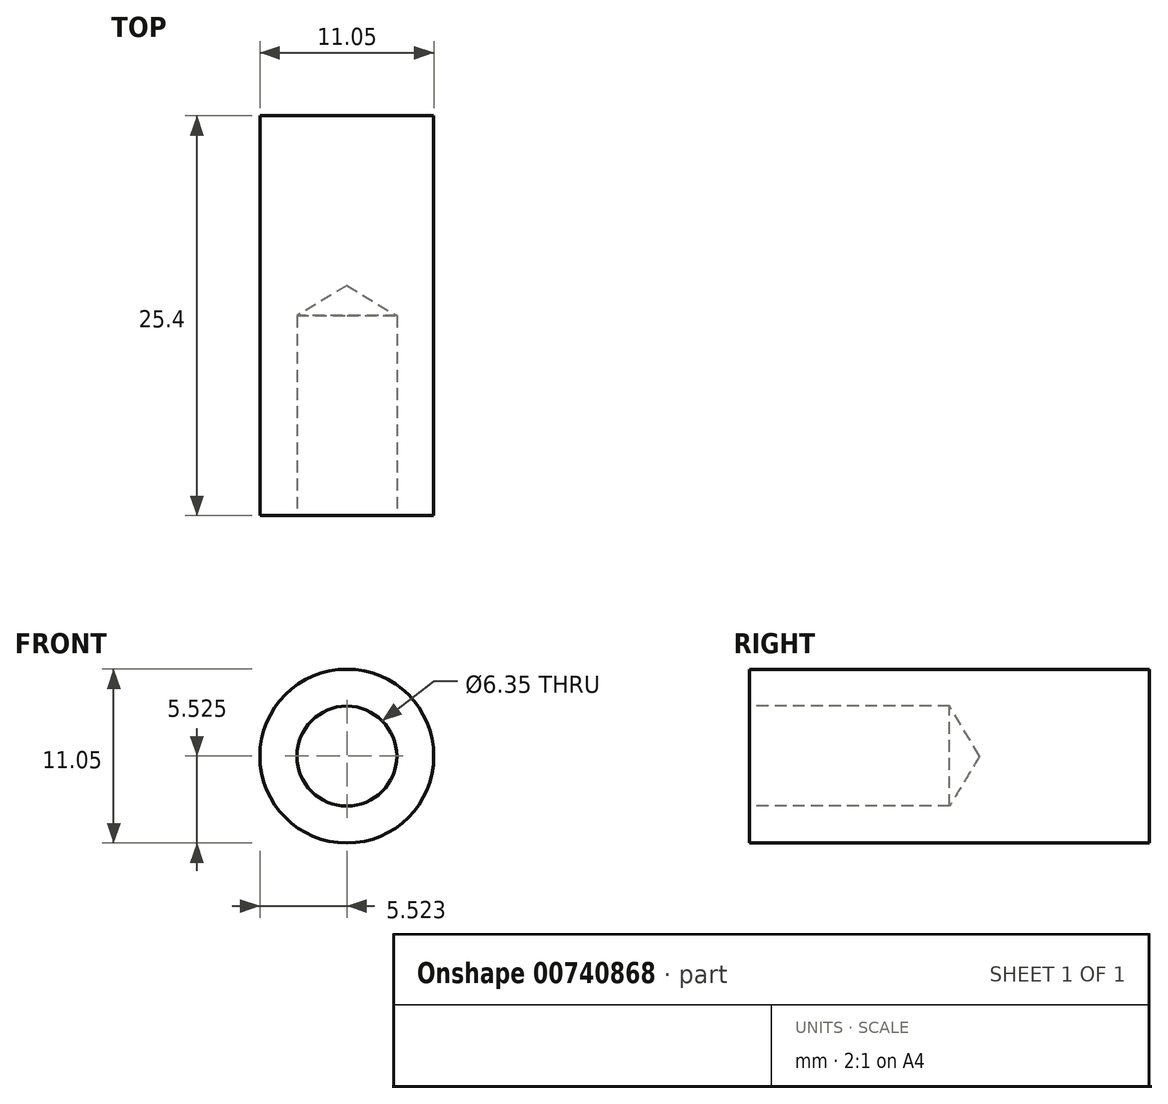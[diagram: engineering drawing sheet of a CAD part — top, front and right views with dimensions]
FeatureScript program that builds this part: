
annotation { "Feature Type Name" : "Feature", "Feature Type Description" : "" }
export const myFeature = defineFeature(function(context is Context, id is Id, definition is map)
    precondition{}
    {
        {
            var Q0;
            Q0=qCreatedBy(makeId("Front.planeOp"),FACE);
            var sketch = newSketch(context, id + "F0", { "sketchPlane" : qUnion([Q0])});
            skCircle(sketch, "E0", {"center": v(32.51, 16.31) * mm, "radius": 5.52 * mm});
            skSolve(sketch);
        }
        {
            var Q0;
            Q0=makeQuery(id+"F0.imprint","IMPRINT",FACE,{"disambiguationData":[TD([[makeQuery(id+"F0.imprint","IMPRINT",EDGE,{"derivedFrom":sQuery(id+"F0.wireOp",EDGE,"E0")}),1.0]])]});
            extrude(context, id + "F1", {"entities" : qUnion([Q0]), "depth" : 25.4 * mm, "offsetDistance" : 25.4 * mm});
        }
        {
            var Q0;
            Q0=makeQuery(id+"F1.opExtrude","CAP_FACE",FACE,{"disambiguationData":[OSD([sQuery(id+"F0.wireOp",EDGE,"E0")])],"isStart":false});
            var sketch = newSketch(context, id + "F2", { "sketchPlane" : qUnion([Q0])});
            skCircle(sketch, "E1", {"center": v(32.51, 16.31) * mm, "radius": 4.73 * mm});
            skSolve(sketch);
        }
        {
            var Q0;
            Q0=sQuery(id+"F2.wireOp",VERTEX,"E1.center");
            var Q1;
            Q1=makeQuery(id+"F1.opExtrude","SWEPT_BODY",BODY,{"disambiguationData":[OSD([sQuery(id+"F0.wireOp",EDGE,"E0")])]});
            hole(context, id + "F3", {"style" : HoleStyle.SIMPLE, "endStyle" : HoleEndStyle.BLIND, "holeDiameter" : 6.35 * mm, "majorDiameter" : 6.35 * mm, "holeDepth" : 12.7 * mm, "isTappedThrough" : true, "tappedDepth" : 12.7 * mm, "tapClearance" : 3, "startFromSketch" : true, "locations" : qUnion([Q0]), "scope" : qUnion([Q1])});
        }
    });
